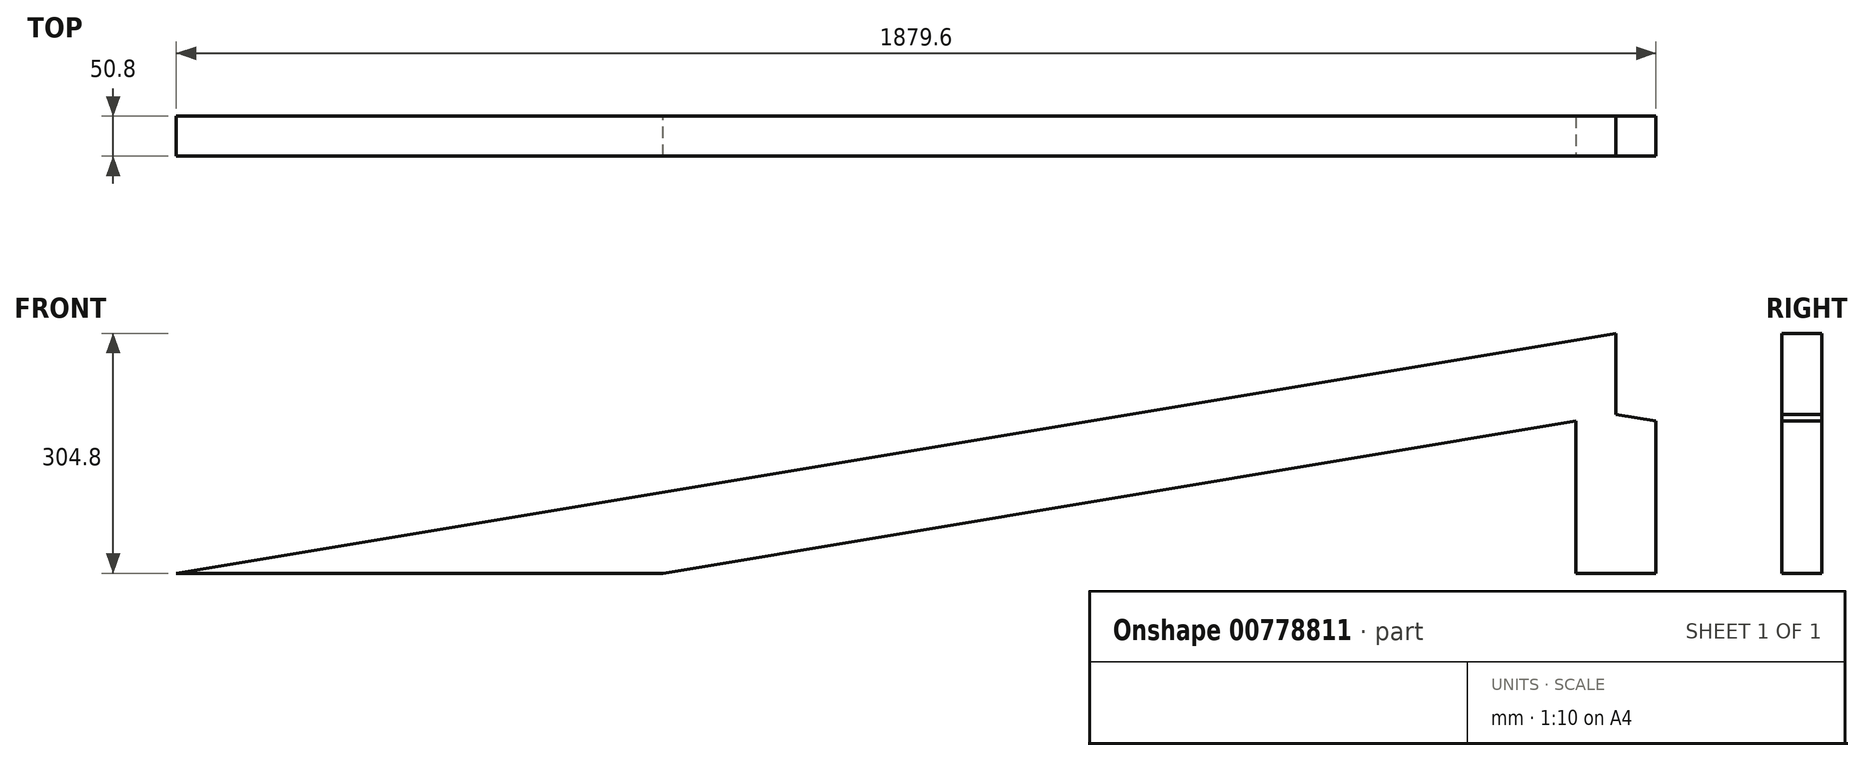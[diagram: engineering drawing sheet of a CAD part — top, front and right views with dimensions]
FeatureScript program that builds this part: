
annotation { "Feature Type Name" : "Feature", "Feature Type Description" : "" }
export const myFeature = defineFeature(function(context is Context, id is Id, definition is map)
    precondition{}
    {
        {
            var Q0;
            Q0=qCreatedBy(makeId("Front.planeOp"),FACE);
            var sketch = newSketch(context, id + "F0", { "sketchPlane" : qUnion([Q0])});
            skLineSegment(sketch, "E0", {"start": v(-1828.8, 0) * mm, "end": v(-1210.8, 0) * mm});
            skLineSegment(sketch, "E1", {"start": v(-1210.8, 0) * mm, "end": v(0, 201.8) * mm});
            skLineSegment(sketch, "E2", {"start": v(0, 201.8) * mm, "end": v(0, 304.8) * mm});
            skLineSegment(sketch, "E3", {"start": v(0, 304.8) * mm, "end": v(-1828.8, 0) * mm});
            skSolve(sketch);
        }
        {
            var Q0;
            Q0 = qSketchRegion(id + "F0", true);
            extrude(context, id + "F1", {"entities" : qUnion([Q0]), "depth" : 50.8 * mm, "offsetDistance" : 25.4 * mm});
        }
        {
            var Q0;
            Q0=makeQuery(id+"F1.opExtrude","CAP_FACE",FACE,{"disambiguationData":[OSD([sQuery(id+"F0.wireOp",EDGE,"E0"),sQuery(id+"F0.wireOp",EDGE,"E1"),sQuery(id+"F0.wireOp",EDGE,"E2"),sQuery(id+"F0.wireOp",EDGE,"E3")])],"isStart":false});
            var sketch = newSketch(context, id + "F2", { "sketchPlane" : qUnion([Q0])});
            skLineSegment(sketch, "E4", {"start": v(0, 201.8) * mm, "end": v(-50.8, 193.33) * mm});
            skLineSegment(sketch, "E5", {"start": v(-50.8, 193.33) * mm, "end": v(-50.8, 0) * mm});
            skLineSegment(sketch, "E6", {"start": v(-50.8, 0) * mm, "end": v(50.8, 0) * mm});
            skLineSegment(sketch, "E7", {"start": v(50.8, 0) * mm, "end": v(50.8, 193.33) * mm});
            skLineSegment(sketch, "E8", {"start": v(50.8, 193.33) * mm, "end": v(0, 201.8) * mm});
            skSolve(sketch);
        }
        {
            var Q0;
            Q0=makeQuery(id+"F2.imprint","IMPRINT",FACE,{"disambiguationData":[TD([[makeQuery(id+"F2.imprint","IMPRINT",EDGE,{"derivedFrom":sQuery(id+"F2.wireOp",EDGE,"E4")}),-1.0]])]});
            extrude(context, id + "F3", {"entities" : qUnion([Q0]), "operationType" : NewBodyOperationType.ADD, "oppositeDirection" : true, "depth" : 50.8 * mm, "offsetDistance" : 25.4 * mm});
        }
    });
